# Revit family: LVSKEY
name_source: partatom
category: Communication Devices
revit_build: Autodesk Revit 2014 (Build: 20130308_1515(x64)
units: mm (PartAtom-declared; Revit-internal decimal feet)

## types (1)
- LVSKEY
    Assembly Code = D5090
    Default Elevation = 48 "
    Description = The Hubbell Control Solutions' Low Voltage Heavy Duty Key Switch is
designed to provide a secure means to manually control lighting in
areas where security or access control are a concern. The center loaded
key action provides an ON with a firm twist of the key to the right and
an OFF with a twist to the left. The key can be removed in the center
position only.
    Environmental Conditions = Indoor Use only, Relative Humidity(Non Condensing) 10%-90%
    Feartures = Attractive brushed stainless steel finish
• Mounts to standard single gang switch box (not provided)
• Connect to NXCI Contact Interface Module (order separately) for CAT5
digital connection to NX Smart Port
• Low voltage Class 2 device
• Connect directly to CX or NX lighting control panels
• Tactile response for ON/OFF contacts
• Provided with two keys
    Housing Material = Metal-Hubbell-Galvanized_Steel
    Manufacturer = Hubbell Control Solutions
    Model = LVKEY
    Product Documentation Link = https://hubbellcdn.com
    Product Page URL = https://www.hubbell.com
    Type Comments = Heavy Duty Key Switch
    URL = https://www.hubbell.com
    Warranty = 5-Years Warranty

## geometry (parser evidence)
native form markers: Sweep x2
no freeform markers — native parametric forms only
